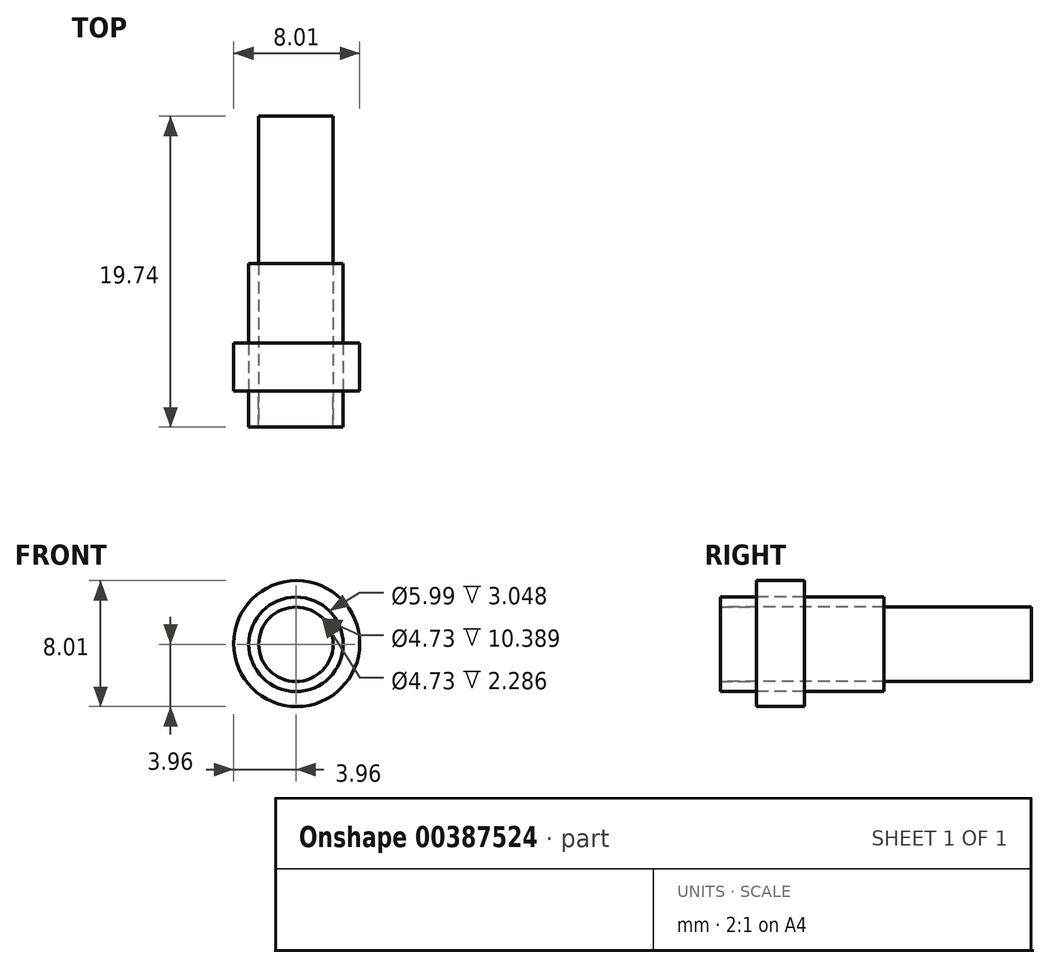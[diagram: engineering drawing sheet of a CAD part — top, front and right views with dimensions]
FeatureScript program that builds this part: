
annotation { "Feature Type Name" : "Feature", "Feature Type Description" : "" }
export const myFeature = defineFeature(function(context is Context, id is Id, definition is map)
    precondition{}
    {
        {
            var Q0;
            Q0=qCreatedBy(makeId("Front.planeOp"),FACE);
            var sketch = newSketch(context, id + "F0", { "sketchPlane" : qUnion([Q0])});
            skCircle(sketch, "E0", {"center": v(0, 0) * mm, "radius": 3 * mm});
            skCircle(sketch, "E1", {"center": v(0.04, 0.04) * mm, "radius": 4 * mm});
            skCircle(sketch, "E2", {"center": v(0, 0) * mm, "radius": 2.36 * mm});
            skSolve(sketch);
        }
        {
            var Q0;
            Q0=makeQuery(id+"F0.imprint","IMPRINT",FACE,{"disambiguationData":[TD([[makeQuery(id+"F0.imprint","IMPRINT",EDGE,{"derivedFrom":sQuery(id+"F0.wireOp",EDGE,"E0")}),1.0]])]});
            extrude(context, id + "F1", {"entities" : qUnion([Q0]), "depth" : 2.3 * mm});
        }
        {
            var Q0;
            Q0=makeQuery(id+"F0.imprint","IMPRINT",FACE,{"disambiguationData":[TD([[makeQuery(id+"F0.imprint","IMPRINT",EDGE,{"derivedFrom":sQuery(id+"F0.wireOp",EDGE,"E0")}),-1.0]])]});
            extrude(context, id + "F2", {"entities" : qUnion([Q0]), "oppositeDirection" : true, "depth" : 3.05 * mm});
        }
        {
            var Q0;
            Q0=makeQuery(id+"F1.opExtrude","CAP_FACE",FACE,{"disambiguationData":[OSD([sQuery(id+"F0.wireOp",EDGE,"E0")])],"isStart":false});
            extrude(context, id + "F3", {"entities" : qUnion([Q0]), "oppositeDirection" : true, "depth" : 10.4 * mm});
        }
        {
            var Q0;
            Q0=makeQuery(id+"F0.imprint","IMPRINT",FACE,{"disambiguationData":[TD([[makeQuery(id+"F0.imprint","IMPRINT",EDGE,{"derivedFrom":sQuery(id+"F0.wireOp",EDGE,"E2")}),1.0]])]});
            extrude(context, id + "F4", {"entities" : qUnion([Q0]), "oppositeDirection" : true, "depth" : 17.45 * mm});
        }
    });
